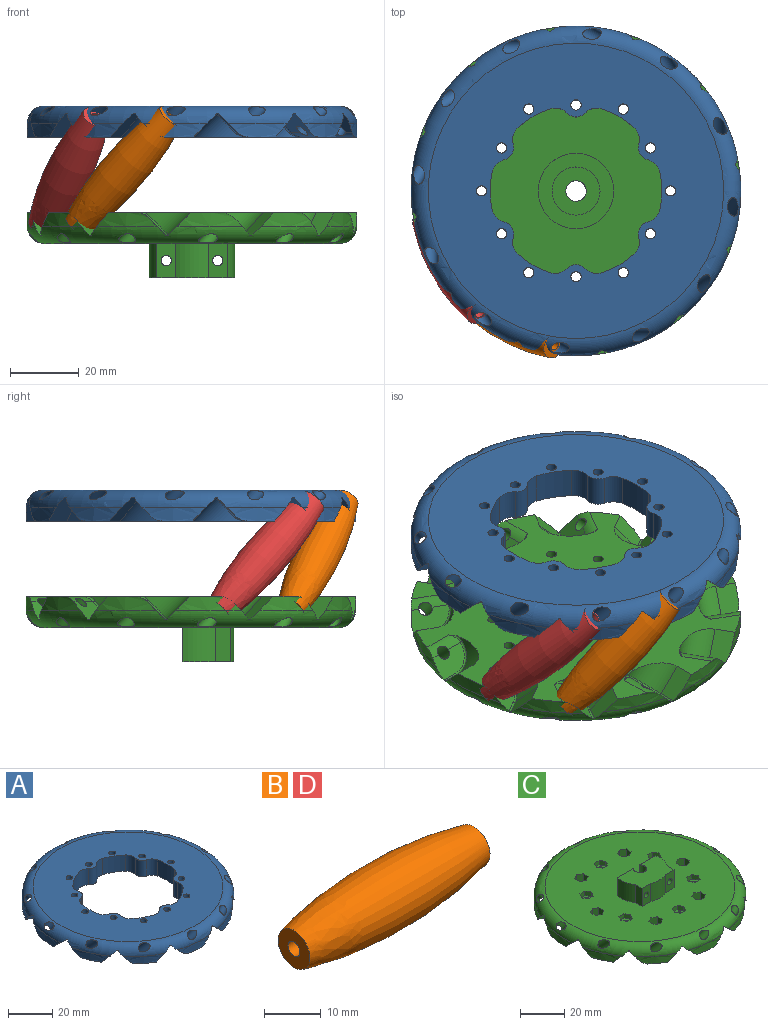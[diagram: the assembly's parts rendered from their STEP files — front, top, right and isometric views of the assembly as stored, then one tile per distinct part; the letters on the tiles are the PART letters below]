
ASSEMBLY  parts=4 mates=4
PART A: 147 faces, bbox 104.2x104.2x17.8 mm
  f0: plane 86x86mm, normal (0,0,1), area 3899.4mm2, adj f9,f111,f112,f113,f114,f115,f116,f117
  f1: cylinder r=48mm len=17.13mm, axis (0,0,1), area 57.6mm2, adj f3,f4,f8,f9,f17
  f2: cylinder r=48mm len=18.65mm, axis (0,0,1), area 57.6mm2, adj f3,f7,f9,f103,f107
  f3: plane 96.26x96.26mm, normal (0,0,-1), area 3132.1mm2, adj f1,f2,f5,f7,f8,f10,f13,f15
  f4: plane 12.07x5.41mm, normal (0,-0.71,-0.71), area 68.4mm2, adj f1,f6,f8,f9,f11,f12
  f5: cylinder r=7.5mm len=13.85mm, axis (0,-0.71,-0.71), area 82.4mm2, adj f3,f7,f10,f11
  f6: cylinder r=2mm len=10.2mm, axis (0,-0.71,-0.71), area 104.3mm2, adj f4,f8,f9
  f7: plane 6.77x6.77mm, normal (0,0.71,-0.71), area 54.3mm2, adj f2,f3,f5,f9,f12
  f8: cylinder r=5mm len=11.15mm, axis (-1,0,0), area 34.3mm2, adj f1,f3,f4,f6,f10
  f9: torus R=43mm, axis (0,0,1), area 1951.1mm2, adj f0,f1,f2,f4,f6,f7,f12,f13
  f10: bspline ~5.43x2.95mm, area 2.6mm2, adj f3,f5,f8,f11
  f11: torus R=7mm, axis (0,-0.71,-0.71), area 9.4mm2, adj f4,f5,f10,f12
  f12: cylinder r=0.5mm len=4.64mm, axis (1,0,0), area 3.6mm2, adj f4,f7,f9,f11
  f13: cylinder r=48mm len=15.17mm, axis (0,0,1), area 57.6mm2, adj f3,f9,f14,f18,f26
  f14: plane 12.74x8.04mm, normal (0.35,-0.61,-0.71), area 68.4mm2, adj f9,f13,f16,f18,f20,f21
  f15: cylinder r=7.5mm len=13.85mm, axis (0.35,-0.61,-0.71), area 82.4mm2, adj f3,f17,f19,f20
  f16: cylinder r=2mm len=10.2mm, axis (0.35,-0.61,-0.71), area 104.3mm2, adj f9,f14,f18
  f17: plane 8.59x8.19mm, normal (-0.35,0.61,-0.71), area 54.3mm2, adj f1,f3,f9,f15,f21
  f18: cylinder r=5mm len=11.43mm, axis (-0.87,-0.5,0), area 34.3mm2, adj f3,f13,f14,f16,f19
  f19: bspline ~5.5x2.95mm, area 2.6mm2, adj f3,f15,f18,f20
  f20: torus R=7mm, axis (0.35,-0.61,-0.71), area 9.4mm2, adj f14,f15,f19,f21
  f21: cylinder r=0.5mm len=4.37mm, axis (0.87,0.5,0), area 3.6mm2, adj f9,f14,f17,f20
  f22: cylinder r=48mm len=18.65mm, axis (0,0,1), area 57.6mm2, adj f3,f9,f23,f27,f35
  f23: plane 10.46x10.46mm, normal (0.61,-0.35,-0.71), area 68.4mm2, adj f9,f22,f25,f27,f29,f30
  f24: cylinder r=7.5mm len=15.56mm, axis (0.61,-0.35,-0.71), area 82.4mm2, adj f3,f26,f28,f29
  f25: cylinder r=2mm len=10.2mm, axis (0.61,-0.35,-0.71), area 104.3mm2, adj f9,f23,f27
  f26: plane 8.86x7.49mm, normal (-0.61,0.35,-0.71), area 54.3mm2, adj f3,f9,f13,f24,f30
  f27: cylinder r=5mm len=11.43mm, axis (-0.5,-0.87,0), area 34.3mm2, adj f3,f22,f23,f25,f28
  f28: bspline ~4.45x3.95mm, area 2.6mm2, adj f3,f24,f27,f29
  f29: torus R=7mm, axis (0.61,-0.35,-0.71), area 9.4mm2, adj f23,f24,f28,f30
  f30: cylinder r=0.5mm len=4.37mm, axis (0.5,0.87,0), area 3.6mm2, adj f9,f23,f26,f29
  f31: cylinder r=48mm len=17.13mm, axis (0,0,1), area 57.6mm2, adj f3,f9,f32,f36,f44
  f32: plane 12.07x5.41mm, normal (0.71,0,-0.71), area 68.4mm2, adj f9,f31,f34,f36,f38,f39
  f33: cylinder r=7.5mm len=13.85mm, axis (0.71,0,-0.71), area 82.4mm2, adj f3,f35,f37,f38
  f34: cylinder r=2mm len=10.2mm, axis (0.71,0,-0.71), area 104.3mm2, adj f9,f32,f36
  f35: plane 6.77x6.77mm, normal (-0.71,0,-0.71), area 54.3mm2, adj f3,f9,f22,f33,f39
  f36: cylinder r=5mm len=11.15mm, axis (0,-1,0), area 34.3mm2, adj f3,f31,f32,f34,f37
  f37: bspline ~5.43x2.95mm, area 2.6mm2, adj f3,f33,f36,f38
  f38: torus R=7mm, axis (0.71,0,-0.71), area 9.4mm2, adj f32,f33,f37,f39
  f39: cylinder r=0.5mm len=4.64mm, axis (0,1,0), area 3.6mm2, adj f9,f32,f35,f38
  f40: cylinder r=48mm len=15.17mm, axis (0,0,1), area 57.6mm2, adj f3,f9,f41,f45,f53
  f41: plane 12.74x8.04mm, normal (0.61,0.35,-0.71), area 68.4mm2, adj f9,f40,f43,f45,f47,f48
  f42: cylinder r=7.5mm len=13.85mm, axis (0.61,0.35,-0.71), area 82.4mm2, adj f3,f44,f46,f47
  f43: cylinder r=2mm len=10.2mm, axis (0.61,0.35,-0.71), area 104.3mm2, adj f9,f41,f45
  f44: plane 8.59x8.19mm, normal (-0.61,-0.35,-0.71), area 54.3mm2, adj f3,f9,f31,f42,f48
  f45: cylinder r=5mm len=11.43mm, axis (0.5,-0.87,0), area 34.3mm2, adj f3,f40,f41,f43,f46
  f46: bspline ~5.5x2.95mm, area 2.6mm2, adj f3,f42,f45,f47
  f47: torus R=7mm, axis (0.61,0.35,-0.71), area 9.4mm2, adj f41,f42,f46,f48
  f48: cylinder r=0.5mm len=4.37mm, axis (-0.5,0.87,0), area 3.6mm2, adj f9,f41,f44,f47
  f49: cylinder r=48mm len=18.65mm, axis (0,0,1), area 57.6mm2, adj f3,f9,f50,f54,f62
  f50: plane 10.46x10.46mm, normal (0.35,0.61,-0.71), area 68.4mm2, adj f9,f49,f52,f54,f56,f57
  f51: cylinder r=7.5mm len=15.56mm, axis (0.35,0.61,-0.71), area 82.4mm2, adj f3,f53,f55,f56
  f52: cylinder r=2mm len=10.2mm, axis (0.35,0.61,-0.71), area 104.3mm2, adj f9,f50,f54
  f53: plane 8.86x7.49mm, normal (-0.35,-0.61,-0.71), area 54.3mm2, adj f3,f9,f40,f51,f57
  f54: cylinder r=5mm len=11.43mm, axis (0.87,-0.5,0), area 34.3mm2, adj f3,f49,f50,f52,f55
  f55: bspline ~4.45x3.95mm, area 2.6mm2, adj f3,f51,f54,f56
  f56: torus R=7mm, axis (0.35,0.61,-0.71), area 9.4mm2, adj f50,f51,f55,f57
  f57: cylinder r=0.5mm len=4.37mm, axis (-0.87,0.5,0), area 3.6mm2, adj f9,f50,f53,f56
  f58: cylinder r=48mm len=17.13mm, axis (0,0,1), area 57.6mm2, adj f3,f9,f59,f63,f71
  f59: plane 12.07x5.41mm, normal (0,0.71,-0.71), area 68.4mm2, adj f9,f58,f61,f63,f65,f66
  f60: cylinder r=7.5mm len=13.85mm, axis (0,0.71,-0.71), area 82.4mm2, adj f3,f62,f64,f65
  f61: cylinder r=2mm len=10.2mm, axis (0,0.71,-0.71), area 104.3mm2, adj f9,f59,f63
  f62: plane 6.77x6.77mm, normal (0,-0.71,-0.71), area 54.3mm2, adj f3,f9,f49,f60,f66
  f63: cylinder r=5mm len=11.15mm, axis (1,0,0), area 34.3mm2, adj f3,f58,f59,f61,f64
  f64: bspline ~5.43x2.95mm, area 2.6mm2, adj f3,f60,f63,f65
  f65: torus R=7mm, axis (0,0.71,-0.71), area 9.4mm2, adj f59,f60,f64,f66
  f66: cylinder r=0.5mm len=4.64mm, axis (-1,0,0), area 3.6mm2, adj f9,f59,f62,f65
  f67: cylinder r=48mm len=15.17mm, axis (0,0,1), area 57.6mm2, adj f3,f9,f68,f72,f80
  f68: plane 12.74x8.04mm, normal (-0.35,0.61,-0.71), area 68.4mm2, adj f9,f67,f70,f72,f74,f75
  f69: cylinder r=7.5mm len=13.85mm, axis (-0.35,0.61,-0.71), area 82.4mm2, adj f3,f71,f73,f74
  f70: cylinder r=2mm len=10.2mm, axis (-0.35,0.61,-0.71), area 104.3mm2, adj f9,f68,f72
  f71: plane 8.59x8.19mm, normal (0.35,-0.61,-0.71), area 54.3mm2, adj f3,f9,f58,f69,f75
  f72: cylinder r=5mm len=11.43mm, axis (0.87,0.5,0), area 34.3mm2, adj f3,f67,f68,f70,f73
  f73: bspline ~5.5x2.95mm, area 2.6mm2, adj f3,f69,f72,f74
  f74: torus R=7mm, axis (-0.35,0.61,-0.71), area 9.4mm2, adj f68,f69,f73,f75
  f75: cylinder r=0.5mm len=4.37mm, axis (-0.87,-0.5,0), area 3.6mm2, adj f9,f68,f71,f74
  f76: cylinder r=48mm len=18.65mm, axis (0,0,1), area 57.6mm2, adj f3,f9,f77,f81,f89
  f77: plane 10.46x10.46mm, normal (-0.61,0.35,-0.71), area 68.4mm2, adj f9,f76,f79,f81,f83,f84
  f78: cylinder r=7.5mm len=15.56mm, axis (-0.61,0.35,-0.71), area 82.4mm2, adj f3,f80,f82,f83
  f79: cylinder r=2mm len=10.2mm, axis (-0.61,0.35,-0.71), area 104.3mm2, adj f9,f77,f81
  f80: plane 8.86x7.49mm, normal (0.61,-0.35,-0.71), area 54.3mm2, adj f3,f9,f67,f78,f84
  f81: cylinder r=5mm len=11.43mm, axis (0.5,0.87,0), area 34.3mm2, adj f3,f76,f77,f79,f82
  f82: bspline ~4.45x3.95mm, area 2.6mm2, adj f3,f78,f81,f83
  f83: torus R=7mm, axis (-0.61,0.35,-0.71), area 9.4mm2, adj f77,f78,f82,f84
  f84: cylinder r=0.5mm len=4.37mm, axis (-0.5,-0.87,0), area 3.6mm2, adj f9,f77,f80,f83
  f85: cylinder r=48mm len=17.13mm, axis (0,0,1), area 57.6mm2, adj f3,f9,f86,f90,f98
  f86: plane 12.07x5.41mm, normal (-0.71,0,-0.71), area 68.4mm2, adj f9,f85,f88,f90,f92,f93
  f87: cylinder r=7.5mm len=13.85mm, axis (-0.71,0,-0.71), area 82.4mm2, adj f3,f89,f91,f92
  f88: cylinder r=2mm len=10.2mm, axis (-0.71,0,-0.71), area 104.3mm2, adj f9,f86,f90
  f89: plane 6.77x6.77mm, normal (0.71,0,-0.71), area 54.3mm2, adj f3,f9,f76,f87,f93
  f90: cylinder r=5mm len=11.15mm, axis (0,1,0), area 34.3mm2, adj f3,f85,f86,f88,f91
  f91: bspline ~5.43x2.95mm, area 2.6mm2, adj f3,f87,f90,f92
  f92: torus R=7mm, axis (-0.71,0,-0.71), area 9.4mm2, adj f86,f87,f91,f93
  f93: cylinder r=0.5mm len=4.64mm, axis (0,-1,0), area 3.6mm2, adj f9,f86,f89,f92
  f94: cylinder r=48mm len=15.17mm, axis (0,0,1), area 57.6mm2, adj f3,f9,f95,f99,f106
  f95: plane 12.74x8.04mm, normal (-0.61,-0.35,-0.71), area 68.4mm2, adj f9,f94,f97,f99,f101,f102
  f96: cylinder r=7.5mm len=13.85mm, axis (-0.61,-0.35,-0.71), area 82.4mm2, adj f3,f98,f100,f101
  f97: cylinder r=2mm len=10.2mm, axis (-0.61,-0.35,-0.71), area 104.3mm2, adj f9,f95,f99
  f98: plane 8.59x8.19mm, normal (0.61,0.35,-0.71), area 54.3mm2, adj f3,f9,f85,f96,f102
  f99: cylinder r=5mm len=11.43mm, axis (-0.5,0.87,0), area 34.3mm2, adj f3,f94,f95,f97,f100
  f100: bspline ~5.5x2.95mm, area 2.6mm2, adj f3,f96,f99,f101
  f101: torus R=7mm, axis (-0.61,-0.35,-0.71), area 9.4mm2, adj f95,f96,f100,f102
  f102: cylinder r=0.5mm len=4.37mm, axis (0.5,-0.87,0), area 3.6mm2, adj f9,f95,f98,f101
  f103: plane 10.46x10.46mm, normal (-0.35,-0.61,-0.71), area 68.4mm2, adj f2,f9,f105,f107,f109,f110
  f104: cylinder r=7.5mm len=15.56mm, axis (-0.35,-0.61,-0.71), area 82.4mm2, adj f3,f106,f108,f109
  f105: cylinder r=2mm len=10.2mm, axis (-0.35,-0.61,-0.71), area 104.3mm2, adj f9,f103,f107
  f106: plane 8.86x7.49mm, normal (0.35,0.61,-0.71), area 54.3mm2, adj f3,f9,f94,f104,f110
  f107: cylinder r=5mm len=11.43mm, axis (-0.87,0.5,0), area 34.3mm2, adj f2,f3,f103,f105,f108
  f108: bspline ~4.45x3.95mm, area 2.6mm2, adj f3,f104,f107,f109
  f109: torus R=7mm, axis (-0.35,-0.61,-0.71), area 9.4mm2, adj f103,f104,f108,f110
  f110: cylinder r=0.5mm len=4.37mm, axis (0.87,-0.5,0), area 3.6mm2, adj f9,f103,f106,f109
  f111: cylinder r=1.5mm len=9mm, axis (0,0,-1), area 84.8mm2, adj f0,f3
  f112: cylinder r=1.5mm len=9mm, axis (0,0,-1), area 84.8mm2, adj f0,f3
  f113: cylinder r=1.5mm len=9mm, axis (0,0,-1), area 84.8mm2, adj f0,f3
  f114: cylinder r=1.5mm len=9mm, axis (0,0,-1), area 84.8mm2, adj f0,f3
  f115: cylinder r=1.5mm len=9mm, axis (0,0,-1), area 84.8mm2, adj f0,f3
  f116: cylinder r=1.5mm len=9mm, axis (0,0,-1), area 84.8mm2, adj f0,f3
  f117: cylinder r=1.5mm len=9mm, axis (0,0,-1), area 84.8mm2, adj f0,f3
  f118: cylinder r=1.5mm len=9mm, axis (0,0,-1), area 84.8mm2, adj f0,f3
  f119: cylinder r=1.5mm len=9mm, axis (0,0,-1), area 84.8mm2, adj f0,f3
  f120: cylinder r=1.5mm len=9mm, axis (0,0,-1), area 84.8mm2, adj f0,f3
  f121: cylinder r=1.5mm len=9mm, axis (0,0,-1), area 84.8mm2, adj f0,f3
  f122: cylinder r=1.5mm len=9mm, axis (0,0,-1), area 84.8mm2, adj f0,f3
  f123: cylinder r=25mm len=10.67mm, axis (0,0,-1), area 96.7mm2, adj f0,f3,f135,f146
  f124: cylinder r=3.5mm len=9mm, axis (0,0,-1), area 50.2mm2, adj f0,f3,f135,f136
  f125: cylinder r=25mm len=9.24mm, axis (0,0,-1), area 96.7mm2, adj f0,f3,f136,f137
  f126: cylinder r=3.5mm len=9mm, axis (0,0,-1), area 50.2mm2, adj f0,f3,f137,f138
  f127: cylinder r=25mm len=9.24mm, axis (0,0,-1), area 96.7mm2, adj f0,f3,f138,f139
  f128: cylinder r=3.5mm len=9mm, axis (0,0,-1), area 50.2mm2, adj f0,f3,f139,f140
  f129: cylinder r=25mm len=10.67mm, axis (0,0,-1), area 96.7mm2, adj f0,f3,f140,f141
  f130: cylinder r=3.5mm len=9mm, axis (0,0,-1), area 50.2mm2, adj f0,f3,f141,f142
  f131: cylinder r=25mm len=9.24mm, axis (0,0,-1), area 96.7mm2, adj f0,f3,f142,f143
  f132: cylinder r=3.5mm len=9mm, axis (0,0,-1), area 50.2mm2, adj f0,f3,f143,f144
  f133: cylinder r=25mm len=9.24mm, axis (0,0,-1), area 96.7mm2, adj f0,f3,f144,f145
  f134: cylinder r=3.5mm len=9mm, axis (0,0,-1), area 50.2mm2, adj f0,f3,f145,f146
  f135: cylinder r=5mm len=9mm, axis (0,0,-1), area 49.7mm2, adj f0,f3,f123,f124
  f136: cylinder r=5mm len=9mm, axis (0,0,-1), area 49.7mm2, adj f0,f3,f124,f125
  f137: cylinder r=5mm len=9mm, axis (0,0,-1), area 49.7mm2, adj f0,f3,f125,f126
  f138: cylinder r=5mm len=9mm, axis (0,0,-1), area 49.7mm2, adj f0,f3,f126,f127
  f139: cylinder r=5mm len=9mm, axis (0,0,-1), area 49.7mm2, adj f0,f3,f127,f128
  f140: cylinder r=5mm len=9mm, axis (0,0,-1), area 49.7mm2, adj f0,f3,f128,f129
  f141: cylinder r=5mm len=9mm, axis (0,0,-1), area 49.7mm2, adj f0,f3,f129,f130
  f142: cylinder r=5mm len=9mm, axis (0,0,-1), area 49.7mm2, adj f0,f3,f130,f131
  f143: cylinder r=5mm len=9mm, axis (0,0,-1), area 49.7mm2, adj f0,f3,f131,f132
  f144: cylinder r=5mm len=9mm, axis (0,0,-1), area 49.7mm2, adj f0,f3,f132,f133
  f145: cylinder r=5mm len=9mm, axis (0,0,-1), area 49.7mm2, adj f0,f3,f133,f134
  f146: cylinder r=5mm len=9mm, axis (0,0,-1), area 49.7mm2, adj f0,f3,f123,f134
PART B: 4 faces, bbox 45x13.2x13.2 mm
  f0: revolved ~45x13.2mm, area 1636.1mm2, adj f1,f3
  f1: plane 8x8mm, normal (-1,0,0), area 43.2mm2, adj f0,f2
  f2: cylinder r=1.5mm len=45mm, axis (1,0,0), area 424.1mm2, adj f1,f3
  f3: plane 8x8mm, normal (1,0,0), area 43.2mm2, adj f0,f2
PART C: 224 faces, bbox 104.2x104.2x26 mm
  f0: plane 86x86mm, normal (0,0,1), area 5170.5mm2, adj f13,f22,f124,f125,f126,f127,f128,f129
  f1: cylinder r=1.5mm len=4mm, axis (0,0,-1), area 37.7mm2, adj f16,f217
  f2: cylinder r=1.5mm len=4mm, axis (0,0,-1), area 37.7mm2, adj f16,f210
  f3: cylinder r=1.5mm len=4mm, axis (0,0,-1), area 37.7mm2, adj f16,f203
  f4: cylinder r=1.5mm len=4mm, axis (0,0,-1), area 37.7mm2, adj f16,f196
  f5: cylinder r=1.5mm len=4mm, axis (0,0,-1), area 37.7mm2, adj f16,f189
  f6: cylinder r=1.5mm len=4mm, axis (0,0,-1), area 37.7mm2, adj f16,f182
  f7: cylinder r=1.5mm len=6.5mm, axis (0,0,-1), area 61.3mm2, adj f16,f175
  f8: cylinder r=1.5mm len=6.5mm, axis (0,0,-1), area 61.3mm2, adj f16,f168
  f9: cylinder r=1.5mm len=6.5mm, axis (0,0,-1), area 61.3mm2, adj f16,f161
  f10: cylinder r=1.5mm len=6.5mm, axis (0,0,-1), area 61.3mm2, adj f16,f154
  f11: cylinder r=1.5mm len=6.5mm, axis (0,0,-1), area 61.3mm2, adj f16,f147
  f12: cylinder r=1.5mm len=6.5mm, axis (0,0,-1), area 61.3mm2, adj f16,f140
  f13: plane 10.36x10mm, normal (0,1,0), area 96.5mm2, adj f0,f125,f132,f133,f135
  f14: cylinder r=48mm len=17.55mm, axis (0,0,1), area 59.4mm2, adj f16,f17,f21,f22,f30
  f15: cylinder r=48mm len=19.06mm, axis (0,0,1), area 59.4mm2, adj f16,f20,f22,f116,f120
  f16: plane 96.24x96.24mm, normal (0,0,-1), area 4624.6mm2, adj f1,f2,f3,f4,f5,f6,f7,f8
  f17: plane 12.12x5.17mm, normal (0,-0.71,-0.71), area 66.8mm2, adj f14,f19,f21,f22,f24,f25
  f18: cylinder r=7.5mm len=13.44mm, axis (0,-0.71,-0.71), area 78.3mm2, adj f16,f20,f23,f24
  f19: cylinder r=2mm len=10.42mm, axis (0,-0.71,-0.71), area 107.7mm2, adj f17,f21,f22
  f20: plane 6.55x6.55mm, normal (0,0.71,-0.71), area 52.9mm2, adj f15,f16,f18,f22,f25
  f21: cylinder r=5mm len=11.29mm, axis (-1,0,0), area 34.2mm2, adj f14,f16,f17,f19,f23
  f22: torus R=43mm, axis (0,0,1), area 1968.4mm2, adj f0,f14,f15,f17,f19,f20,f25,f26
  f23: bspline ~5.36x2.96mm, area 2.6mm2, adj f16,f18,f21,f24
  f24: torus R=7mm, axis (0,-0.71,-0.71), area 9.2mm2, adj f17,f18,f23,f25
  f25: cylinder r=0.5mm len=4.8mm, axis (1,0,0), area 3.7mm2, adj f17,f20,f22,f24
  f26: cylinder r=48mm len=15.46mm, axis (0,0,1), area 59.4mm2, adj f16,f22,f27,f31,f39
  f27: plane 12.77x7.88mm, normal (0.35,-0.61,-0.71), area 66.8mm2, adj f22,f26,f29,f31,f33,f34
  f28: cylinder r=7.5mm len=13.44mm, axis (0.35,-0.61,-0.71), area 78.3mm2, adj f16,f30,f32,f33
  f29: cylinder r=2mm len=10.42mm, axis (0.35,-0.61,-0.71), area 107.7mm2, adj f22,f27,f31
  f30: plane 8.47x8.08mm, normal (-0.35,0.61,-0.71), area 52.9mm2, adj f14,f16,f22,f28,f34
  f31: cylinder r=5mm len=11.54mm, axis (-0.87,-0.5,0), area 34.2mm2, adj f16,f26,f27,f29,f32
  f32: bspline ~5.31x2.96mm, area 2.6mm2, adj f16,f28,f31,f33
  f33: torus R=7mm, axis (0.35,-0.61,-0.71), area 9.2mm2, adj f27,f28,f32,f34
  f34: cylinder r=0.5mm len=4.51mm, axis (0.87,0.5,0), area 3.7mm2, adj f22,f27,f30,f33
  f35: cylinder r=48mm len=19.06mm, axis (0,0,1), area 59.4mm2, adj f16,f22,f36,f40,f48
  f36: plane 10.42x10.34mm, normal (0.61,-0.35,-0.71), area 66.8mm2, adj f22,f35,f38,f40,f42,f43
  f37: cylinder r=7.5mm len=15.25mm, axis (0.61,-0.35,-0.71), area 78.3mm2, adj f16,f39,f41,f42
  f38: cylinder r=2mm len=10.42mm, axis (0.61,-0.35,-0.71), area 107.7mm2, adj f22,f36,f40
  f39: plane 8.67x7.48mm, normal (-0.61,0.35,-0.71), area 52.9mm2, adj f16,f22,f26,f37,f43
  f40: cylinder r=5mm len=11.54mm, axis (-0.5,-0.87,0), area 34.2mm2, adj f16,f35,f36,f38,f41
  f41: bspline ~4.17x4.04mm, area 2.6mm2, adj f16,f37,f40,f42
  f42: torus R=7mm, axis (0.61,-0.35,-0.71), area 9.2mm2, adj f36,f37,f41,f43
  f43: cylinder r=0.5mm len=4.51mm, axis (0.5,0.87,0), area 3.7mm2, adj f22,f36,f39,f42
  f44: cylinder r=48mm len=17.55mm, axis (0,0,1), area 59.4mm2, adj f16,f22,f45,f49,f57
  f45: plane 12.12x5.17mm, normal (0.71,0,-0.71), area 66.8mm2, adj f22,f44,f47,f49,f51,f52
  f46: cylinder r=7.5mm len=13.44mm, axis (0.71,0,-0.71), area 78.3mm2, adj f16,f48,f50,f51
  f47: cylinder r=2mm len=10.42mm, axis (0.71,0,-0.71), area 107.7mm2, adj f22,f45,f49
  f48: plane 6.55x6.55mm, normal (-0.71,0,-0.71), area 52.9mm2, adj f16,f22,f35,f46,f52
  f49: cylinder r=5mm len=11.29mm, axis (0,-1,0), area 34.2mm2, adj f16,f44,f45,f47,f50
  f50: bspline ~5.36x2.96mm, area 2.6mm2, adj f16,f46,f49,f51
  f51: torus R=7mm, axis (0.71,0,-0.71), area 9.2mm2, adj f45,f46,f50,f52
  f52: cylinder r=0.5mm len=4.8mm, axis (0,1,0), area 3.7mm2, adj f22,f45,f48,f51
  f53: cylinder r=48mm len=15.46mm, axis (0,0,1), area 59.4mm2, adj f16,f22,f54,f58,f66
  f54: plane 12.77x7.88mm, normal (0.61,0.35,-0.71), area 66.8mm2, adj f22,f53,f56,f58,f60,f61
  f55: cylinder r=7.5mm len=13.44mm, axis (0.61,0.35,-0.71), area 78.3mm2, adj f16,f57,f59,f60
  f56: cylinder r=2mm len=10.42mm, axis (0.61,0.35,-0.71), area 107.7mm2, adj f22,f54,f58
  f57: plane 8.47x8.08mm, normal (-0.61,-0.35,-0.71), area 52.9mm2, adj f16,f22,f44,f55,f61
  f58: cylinder r=5mm len=11.54mm, axis (0.5,-0.87,0), area 34.2mm2, adj f16,f53,f54,f56,f59
  f59: bspline ~5.31x2.96mm, area 2.6mm2, adj f16,f55,f58,f60
  f60: torus R=7mm, axis (0.61,0.35,-0.71), area 9.2mm2, adj f54,f55,f59,f61
  f61: cylinder r=0.5mm len=4.51mm, axis (-0.5,0.87,0), area 3.7mm2, adj f22,f54,f57,f60
  f62: cylinder r=48mm len=19.06mm, axis (0,0,1), area 59.4mm2, adj f16,f22,f63,f67,f75
  f63: plane 10.42x10.34mm, normal (0.35,0.61,-0.71), area 66.8mm2, adj f22,f62,f65,f67,f69,f70
  f64: cylinder r=7.5mm len=15.25mm, axis (0.35,0.61,-0.71), area 78.3mm2, adj f16,f66,f68,f69
  f65: cylinder r=2mm len=10.42mm, axis (0.35,0.61,-0.71), area 107.7mm2, adj f22,f63,f67
  f66: plane 8.67x7.48mm, normal (-0.35,-0.61,-0.71), area 52.9mm2, adj f16,f22,f53,f64,f70
  f67: cylinder r=5mm len=11.54mm, axis (0.87,-0.5,0), area 34.2mm2, adj f16,f62,f63,f65,f68
  f68: bspline ~4.17x4.04mm, area 2.6mm2, adj f16,f64,f67,f69
  f69: torus R=7mm, axis (0.35,0.61,-0.71), area 9.2mm2, adj f63,f64,f68,f70
  f70: cylinder r=0.5mm len=4.51mm, axis (-0.87,0.5,0), area 3.7mm2, adj f22,f63,f66,f69
  f71: cylinder r=48mm len=17.55mm, axis (0,0,1), area 59.4mm2, adj f16,f22,f72,f76,f84
  f72: plane 12.12x5.17mm, normal (0,0.71,-0.71), area 66.8mm2, adj f22,f71,f74,f76,f78,f79
  f73: cylinder r=7.5mm len=13.44mm, axis (0,0.71,-0.71), area 78.3mm2, adj f16,f75,f77,f78
  f74: cylinder r=2mm len=10.42mm, axis (0,0.71,-0.71), area 107.7mm2, adj f22,f72,f76
  f75: plane 6.55x6.55mm, normal (0,-0.71,-0.71), area 52.9mm2, adj f16,f22,f62,f73,f79
  f76: cylinder r=5mm len=11.29mm, axis (1,0,0), area 34.2mm2, adj f16,f71,f72,f74,f77
  f77: bspline ~5.36x2.96mm, area 2.6mm2, adj f16,f73,f76,f78
  f78: torus R=7mm, axis (0,0.71,-0.71), area 9.2mm2, adj f72,f73,f77,f79
  f79: cylinder r=0.5mm len=4.8mm, axis (-1,0,0), area 3.7mm2, adj f22,f72,f75,f78
  f80: cylinder r=48mm len=15.46mm, axis (0,0,1), area 59.4mm2, adj f16,f22,f81,f85,f93
  f81: plane 12.77x7.88mm, normal (-0.35,0.61,-0.71), area 66.8mm2, adj f22,f80,f83,f85,f87,f88
  f82: cylinder r=7.5mm len=13.44mm, axis (-0.35,0.61,-0.71), area 78.3mm2, adj f16,f84,f86,f87
  f83: cylinder r=2mm len=10.42mm, axis (-0.35,0.61,-0.71), area 107.7mm2, adj f22,f81,f85
  f84: plane 8.47x8.08mm, normal (0.35,-0.61,-0.71), area 52.9mm2, adj f16,f22,f71,f82,f88
  f85: cylinder r=5mm len=11.54mm, axis (0.87,0.5,0), area 34.2mm2, adj f16,f80,f81,f83,f86
  f86: bspline ~5.31x2.96mm, area 2.6mm2, adj f16,f82,f85,f87
  f87: torus R=7mm, axis (-0.35,0.61,-0.71), area 9.2mm2, adj f81,f82,f86,f88
  f88: cylinder r=0.5mm len=4.51mm, axis (-0.87,-0.5,0), area 3.7mm2, adj f22,f81,f84,f87
  f89: cylinder r=48mm len=19.06mm, axis (0,0,1), area 59.4mm2, adj f16,f22,f90,f94,f102
  f90: plane 10.42x10.34mm, normal (-0.61,0.35,-0.71), area 66.8mm2, adj f22,f89,f92,f94,f96,f97
  f91: cylinder r=7.5mm len=15.25mm, axis (-0.61,0.35,-0.71), area 78.3mm2, adj f16,f93,f95,f96
  f92: cylinder r=2mm len=10.42mm, axis (-0.61,0.35,-0.71), area 107.7mm2, adj f22,f90,f94
  f93: plane 8.67x7.48mm, normal (0.61,-0.35,-0.71), area 52.9mm2, adj f16,f22,f80,f91,f97
  f94: cylinder r=5mm len=11.54mm, axis (0.5,0.87,0), area 34.2mm2, adj f16,f89,f90,f92,f95
  f95: bspline ~4.17x4.04mm, area 2.6mm2, adj f16,f91,f94,f96
  f96: torus R=7mm, axis (-0.61,0.35,-0.71), area 9.2mm2, adj f90,f91,f95,f97
  f97: cylinder r=0.5mm len=4.51mm, axis (-0.5,-0.87,0), area 3.7mm2, adj f22,f90,f93,f96
  f98: cylinder r=48mm len=17.55mm, axis (0,0,1), area 59.4mm2, adj f16,f22,f99,f103,f111
  f99: plane 12.12x5.17mm, normal (-0.71,0,-0.71), area 66.8mm2, adj f22,f98,f101,f103,f105,f106
  f100: cylinder r=7.5mm len=13.44mm, axis (-0.71,0,-0.71), area 78.3mm2, adj f16,f102,f104,f105
  f101: cylinder r=2mm len=10.42mm, axis (-0.71,0,-0.71), area 107.7mm2, adj f22,f99,f103
  f102: plane 6.55x6.55mm, normal (0.71,0,-0.71), area 52.9mm2, adj f16,f22,f89,f100,f106
  f103: cylinder r=5mm len=11.29mm, axis (0,1,0), area 34.2mm2, adj f16,f98,f99,f101,f104
  f104: bspline ~5.36x2.96mm, area 2.6mm2, adj f16,f100,f103,f105
  f105: torus R=7mm, axis (-0.71,0,-0.71), area 9.2mm2, adj f99,f100,f104,f106
  f106: cylinder r=0.5mm len=4.8mm, axis (0,-1,0), area 3.7mm2, adj f22,f99,f102,f105
  f107: cylinder r=48mm len=15.46mm, axis (0,0,1), area 59.4mm2, adj f16,f22,f108,f112,f119
  f108: plane 12.77x7.88mm, normal (-0.61,-0.35,-0.71), area 66.8mm2, adj f22,f107,f110,f112,f114,f115
  f109: cylinder r=7.5mm len=13.44mm, axis (-0.61,-0.35,-0.71), area 78.3mm2, adj f16,f111,f113,f114
  f110: cylinder r=2mm len=10.42mm, axis (-0.61,-0.35,-0.71), area 107.7mm2, adj f22,f108,f112
  f111: plane 8.47x8.08mm, normal (0.61,0.35,-0.71), area 52.9mm2, adj f16,f22,f98,f109,f115
  f112: cylinder r=5mm len=11.54mm, axis (-0.5,0.87,0), area 34.2mm2, adj f16,f107,f108,f110,f113
  f113: bspline ~5.31x2.96mm, area 2.6mm2, adj f16,f109,f112,f114
  f114: torus R=7mm, axis (-0.61,-0.35,-0.71), area 9.2mm2, adj f108,f109,f113,f115
  f115: cylinder r=0.5mm len=4.51mm, axis (0.5,-0.87,0), area 3.7mm2, adj f22,f108,f111,f114
  f116: plane 10.42x10.34mm, normal (-0.35,-0.61,-0.71), area 66.8mm2, adj f15,f22,f118,f120,f122,f123
  f117: cylinder r=7.5mm len=15.25mm, axis (-0.35,-0.61,-0.71), area 78.3mm2, adj f16,f119,f121,f122
  f118: cylinder r=2mm len=10.42mm, axis (-0.35,-0.61,-0.71), area 107.7mm2, adj f22,f116,f120
  f119: plane 8.67x7.48mm, normal (0.35,0.61,-0.71), area 52.9mm2, adj f16,f22,f107,f117,f123
  f120: cylinder r=5mm len=11.54mm, axis (-0.87,0.5,0), area 34.2mm2, adj f15,f16,f116,f118,f121
  f121: bspline ~4.17x4.04mm, area 2.6mm2, adj f16,f117,f120,f122
  f122: torus R=7mm, axis (-0.35,-0.61,-0.71), area 9.2mm2, adj f116,f117,f121,f123
  f123: cylinder r=0.5mm len=4.51mm, axis (0.87,-0.5,0), area 3.7mm2, adj f22,f116,f119,f122
  f124: plane 10.36x10mm, normal (0,1,0), area 96.5mm2, adj f0,f131,f132,f133,f134
  f125: cylinder r=12.5mm len=10mm, axis (0,0,-1), area 99.3mm2, adj f0,f13,f126,f132
  f126: plane 10x4.41mm, normal (-1,0,0), area 44.1mm2, adj f0,f125,f127,f132
  f127: plane 10x5.5mm, normal (0,-1,0), area 47.9mm2, adj f0,f126,f128,f132,f135
  f128: cylinder r=12.5mm len=10mm, axis (0,0,-1), area 97.4mm2, adj f0,f127,f129,f132
  f129: plane 10x5.5mm, normal (0,-1,0), area 47.9mm2, adj f0,f128,f130,f132,f134
  f130: plane 10x4.41mm, normal (1,0,0), area 44.1mm2, adj f0,f129,f131,f132
  f131: cylinder r=12.5mm len=10mm, axis (0,0,-1), area 99.3mm2, adj f0,f124,f130,f132
  f132: plane 25x14.8mm, normal (0,0,1), area 295.6mm2, adj f13,f124,f125,f126,f127,f128,f129,f130
  f133: cylinder r=3mm len=14mm, axis (0,0,1), area 222.1mm2, adj f0,f13,f124,f132,f136
  f134: cylinder r=1.5mm len=13.86mm, axis (0,-1,0), area 130.6mm2, adj f124,f129
  f135: cylinder r=1.5mm len=13.86mm, axis (0,-1,0), area 130.6mm2, adj f13,f127
  f136: plane 14x14mm, normal (0,0,-1), area 125.7mm2, adj f133,f137
  f137: cylinder r=7mm len=14mm, axis (0,0,-1), area 88mm2, adj f136,f138
  f138: plane 22x22mm, normal (0,0,-1), area 226.2mm2, adj f137,f139
  f139: cylinder r=11mm len=22mm, axis (0,0,-1), area 207.3mm2, adj f16,f138
  f140: plane 6.35x5.5mm, normal (0,0,1), area 19.1mm2, adj f12,f141,f142,f143,f144,f145,f146
  f141: plane 2.75x2.5mm, normal (-0.87,-0.5,0), area 7.9mm2, adj f0,f140,f142,f146
  f142: plane 3.18x2.5mm, normal (0,-1,0), area 7.9mm2, adj f0,f140,f141,f143
  f143: plane 2.75x2.5mm, normal (0.87,-0.5,0), area 7.9mm2, adj f0,f140,f142,f144
  f144: plane 2.75x2.5mm, normal (0.87,0.5,0), area 7.9mm2, adj f0,f140,f143,f145
  f145: plane 3.18x2.5mm, normal (0,1,0), area 7.9mm2, adj f0,f140,f144,f146
  f146: plane 2.75x2.5mm, normal (-0.87,0.5,0), area 7.9mm2, adj f0,f140,f141,f145
  f147: plane 6.35x5.5mm, normal (0,0,1), area 19.1mm2, adj f11,f148,f149,f150,f151,f152,f153
  f148: plane 2.75x2.5mm, normal (-0.87,-0.5,0), area 7.9mm2, adj f0,f147,f149,f153
  f149: plane 3.18x2.5mm, normal (0,-1,0), area 7.9mm2, adj f0,f147,f148,f150
  f150: plane 2.75x2.5mm, normal (0.87,-0.5,0), area 7.9mm2, adj f0,f147,f149,f151
  f151: plane 2.75x2.5mm, normal (0.87,0.5,0), area 7.9mm2, adj f0,f147,f150,f152
  f152: plane 3.18x2.5mm, normal (0,1,0), area 7.9mm2, adj f0,f147,f151,f153
  f153: plane 2.75x2.5mm, normal (-0.87,0.5,0), area 7.9mm2, adj f0,f147,f148,f152
  f154: plane 6.35x5.5mm, normal (0,0,1), area 19.1mm2, adj f10,f155,f156,f157,f158,f159,f160
  f155: plane 2.75x2.5mm, normal (-0.87,0.5,0), area 7.9mm2, adj f0,f154,f156,f160
  f156: plane 2.75x2.5mm, normal (-0.87,-0.5,0), area 7.9mm2, adj f0,f154,f155,f157
  f157: plane 3.18x2.5mm, normal (0,-1,0), area 7.9mm2, adj f0,f154,f156,f158
  f158: plane 2.75x2.5mm, normal (0.87,-0.5,0), area 7.9mm2, adj f0,f154,f157,f159
  f159: plane 2.75x2.5mm, normal (0.87,0.5,0), area 7.9mm2, adj f0,f154,f158,f160
  f160: plane 3.18x2.5mm, normal (0,1,0), area 7.9mm2, adj f0,f154,f155,f159
  f161: plane 6.35x5.5mm, normal (0,0,1), area 19.1mm2, adj f9,f162,f163,f164,f165,f166,f167
  f162: plane 3.18x2.5mm, normal (0,1,0), area 7.9mm2, adj f0,f161,f163,f167
  f163: plane 2.75x2.5mm, normal (-0.87,0.5,0), area 7.9mm2, adj f0,f161,f162,f164
  f164: plane 2.75x2.5mm, normal (-0.87,-0.5,0), area 7.9mm2, adj f0,f161,f163,f165
  f165: plane 3.18x2.5mm, normal (0,-1,0), area 7.9mm2, adj f0,f161,f164,f166
  f166: plane 2.75x2.5mm, normal (0.87,-0.5,0), area 7.9mm2, adj f0,f161,f165,f167
  f167: plane 2.75x2.5mm, normal (0.87,0.5,0), area 7.9mm2, adj f0,f161,f162,f166
  f168: plane 6.35x5.5mm, normal (0,0,1), area 19.1mm2, adj f8,f169,f170,f171,f172,f173,f174
  f169: plane 2.75x2.5mm, normal (0.87,0.5,0), area 7.9mm2, adj f0,f168,f170,f174
  f170: plane 3.18x2.5mm, normal (0,1,0), area 7.9mm2, adj f0,f168,f169,f171
  f171: plane 2.75x2.5mm, normal (-0.87,0.5,0), area 7.9mm2, adj f0,f168,f170,f172
  f172: plane 2.75x2.5mm, normal (-0.87,-0.5,0), area 7.9mm2, adj f0,f168,f171,f173
  f173: plane 3.18x2.5mm, normal (0,-1,0), area 7.9mm2, adj f0,f168,f172,f174
  f174: plane 2.75x2.5mm, normal (0.87,-0.5,0), area 7.9mm2, adj f0,f168,f169,f173
  f175: plane 6.35x5.5mm, normal (0,0,1), area 19.1mm2, adj f7,f176,f177,f178,f179,f180,f181
  f176: plane 2.75x2.5mm, normal (0.87,-0.5,0), area 7.9mm2, adj f0,f175,f177,f181
  f177: plane 2.75x2.5mm, normal (0.87,0.5,0), area 7.9mm2, adj f0,f175,f176,f178
  f178: plane 3.18x2.5mm, normal (0,1,0), area 7.9mm2, adj f0,f175,f177,f179
  f179: plane 2.75x2.5mm, normal (-0.87,0.5,0), area 7.9mm2, adj f0,f175,f178,f180
  f180: plane 2.75x2.5mm, normal (-0.87,-0.5,0), area 7.9mm2, adj f0,f175,f179,f181
  f181: plane 3.18x2.5mm, normal (0,-1,0), area 7.9mm2, adj f0,f175,f176,f180
  f182: plane 6.35x5.5mm, normal (0,0,1), area 19.1mm2, adj f6,f183,f184,f185,f186,f187,f188
  f183: plane 5x2.75mm, normal (0.5,0.87,0), area 15.9mm2, adj f0,f182,f184,f188
  f184: plane 5x2.75mm, normal (-0.5,0.87,0), area 15.9mm2, adj f0,f182,f183,f185
  f185: plane 5x3.18mm, normal (-1,0,0), area 15.9mm2, adj f0,f182,f184,f186
  f186: plane 5x2.75mm, normal (-0.5,-0.87,0), area 15.9mm2, adj f0,f182,f185,f187
  f187: plane 5x2.75mm, normal (0.5,-0.87,0), area 15.9mm2, adj f0,f182,f186,f188
  f188: plane 5x3.18mm, normal (1,0,0), area 15.9mm2, adj f0,f182,f183,f187
  f189: plane 6.35x5.5mm, normal (0,0,1), area 19.1mm2, adj f5,f190,f191,f192,f193,f194,f195
  f190: plane 5x3.18mm, normal (-1,0,0), area 15.9mm2, adj f0,f189,f191,f195
  f191: plane 5x2.75mm, normal (-0.5,-0.87,0), area 15.9mm2, adj f0,f189,f190,f192
  f192: plane 5x2.75mm, normal (0.5,-0.87,0), area 15.9mm2, adj f0,f189,f191,f193
  f193: plane 5x3.18mm, normal (1,0,0), area 15.9mm2, adj f0,f189,f192,f194
  f194: plane 5x2.75mm, normal (0.5,0.87,0), area 15.9mm2, adj f0,f189,f193,f195
  f195: plane 5x2.75mm, normal (-0.5,0.87,0), area 15.9mm2, adj f0,f189,f190,f194
  f196: plane 6.35x5.5mm, normal (0,0,1), area 19.1mm2, adj f4,f197,f198,f199,f200,f201,f202
  f197: plane 5x3.18mm, normal (-1,0,0), area 15.9mm2, adj f0,f196,f198,f202
  f198: plane 5x2.75mm, normal (-0.5,-0.87,0), area 15.9mm2, adj f0,f196,f197,f199
  f199: plane 5x2.75mm, normal (0.5,-0.87,0), area 15.9mm2, adj f0,f196,f198,f200
  f200: plane 5x3.18mm, normal (1,0,0), area 15.9mm2, adj f0,f196,f199,f201
  f201: plane 5x2.75mm, normal (0.5,0.87,0), area 15.9mm2, adj f0,f196,f200,f202
  f202: plane 5x2.75mm, normal (-0.5,0.87,0), area 15.9mm2, adj f0,f196,f197,f201
  f203: plane 6.35x5.5mm, normal (0,0,1), area 19.1mm2, adj f3,f204,f205,f206,f207,f208,f209
  f204: plane 5x2.75mm, normal (-0.5,-0.87,0), area 15.9mm2, adj f0,f203,f205,f209
  f205: plane 5x2.75mm, normal (0.5,-0.87,0), area 15.9mm2, adj f0,f203,f204,f206
  f206: plane 5x3.18mm, normal (1,0,0), area 15.9mm2, adj f0,f203,f205,f207
  f207: plane 5x2.75mm, normal (0.5,0.87,0), area 15.9mm2, adj f0,f203,f206,f208
  f208: plane 5x2.75mm, normal (-0.5,0.87,0), area 15.9mm2, adj f0,f203,f207,f209
  f209: plane 5x3.18mm, normal (-1,0,0), area 15.9mm2, adj f0,f203,f204,f208
  f210: plane 6.35x5.5mm, normal (0,0,1), area 19.1mm2, adj f2,f211,f212,f213,f214,f215,f216
  f211: plane 5x2.75mm, normal (0.5,-0.87,0), area 15.9mm2, adj f0,f210,f212,f216
  f212: plane 5x3.18mm, normal (1,0,0), area 15.9mm2, adj f0,f210,f211,f213
  f213: plane 5x2.75mm, normal (0.5,0.87,0), area 15.9mm2, adj f0,f210,f212,f214
  f214: plane 5x2.75mm, normal (-0.5,0.87,0), area 15.9mm2, adj f0,f210,f213,f215
  f215: plane 5x3.18mm, normal (-1,0,0), area 15.9mm2, adj f0,f210,f214,f216
  f216: plane 5x2.75mm, normal (-0.5,-0.87,0), area 15.9mm2, adj f0,f210,f211,f215
  f217: plane 6.35x5.5mm, normal (0,0,1), area 19.1mm2, adj f1,f218,f219,f220,f221,f222,f223
  f218: plane 5x3.18mm, normal (1,0,0), area 15.9mm2, adj f0,f217,f219,f223
  f219: plane 5x2.75mm, normal (0.5,0.87,0), area 15.9mm2, adj f0,f217,f218,f220
  f220: plane 5x2.75mm, normal (-0.5,0.87,0), area 15.9mm2, adj f0,f217,f219,f221
  f221: plane 5x3.18mm, normal (-1,0,0), area 15.9mm2, adj f0,f217,f220,f222
  f222: plane 5x2.75mm, normal (-0.5,-0.87,0), area 15.9mm2, adj f0,f217,f221,f223
  f223: plane 5x2.75mm, normal (0.5,-0.87,0), area 15.9mm2, adj f0,f217,f218,f222
PART D: same geometry as B
PLACE A at identity fixed
PLACE B rot(axis=(0.39,-0.89,-0.23),57.1deg) t=(-19.97,-36.98,-18.8)mm
PLACE C rot(axis=(0,1,0),180deg) t=(0,0,-40)mm
PLACE D rot(axis=(0.43,-0.84,-0.33),78.2deg) t=(-35.9,-21.83,-19.05)mm
MATE cylindrical D.f2 <-> A.f69  axis (-0.35,0.61,-0.71) through (-43.86,-8.05,-34.96)mm
MATE cylindrical A.f123 <-> C.f133  axis (0,0,1) through (0,0,0)mm
MATE cylindrical A.f33 <-> C.f46  axis (0.71,0,-0.71) through (-20.21,42.01,0.21)mm
MATE cylindrical B.f2 <-> A.f83  axis (0.61,-0.35,0.71) through (-33.74,-29.02,-34.71)mm
